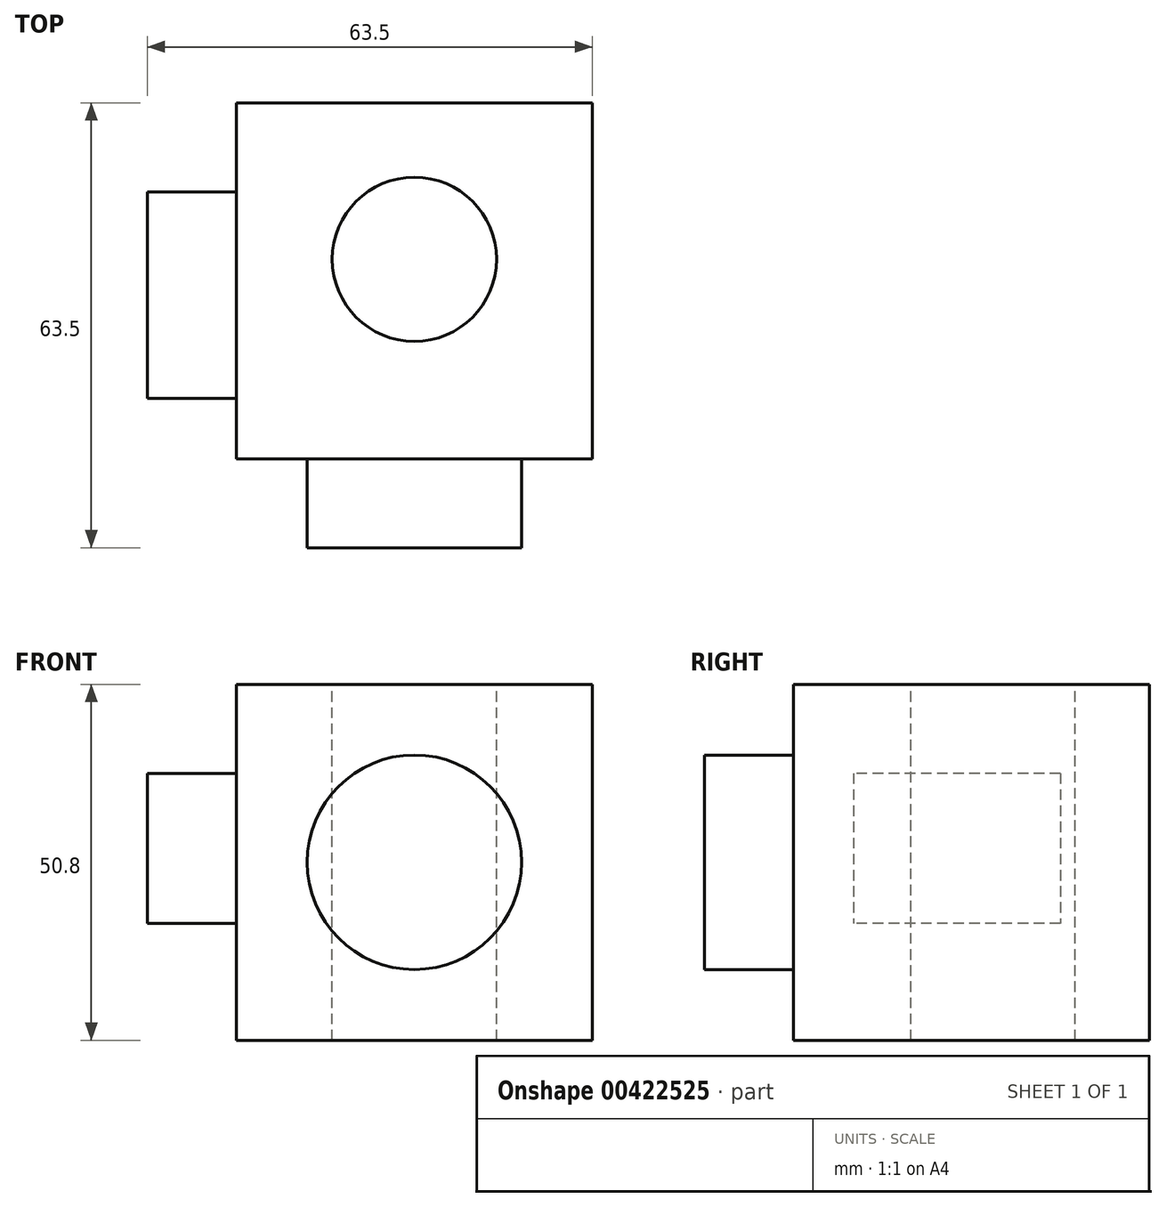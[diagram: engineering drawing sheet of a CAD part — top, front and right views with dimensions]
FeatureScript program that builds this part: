
annotation { "Feature Type Name" : "Feature", "Feature Type Description" : "" }
export const myFeature = defineFeature(function(context is Context, id is Id, definition is map)
    precondition{}
    {
        {
            var Q0;
            Q0=qCreatedBy(makeId("Front.planeOp"),FACE);
            var sketch = newSketch(context, id + "F0", { "sketchPlane" : qUnion([Q0])});
            skLineSegment(sketch, "E0", {"start": v(0, 0) * mm, "end": v(0, 50.8) * mm});
            skLineSegment(sketch, "E1", {"start": v(0, 50.8) * mm, "end": v(50.8, 50.8) * mm});
            skLineSegment(sketch, "E2", {"start": v(50.8, 50.8) * mm, "end": v(50.8, 0) * mm});
            skLineSegment(sketch, "E3", {"start": v(0, 0) * mm, "end": v(50.8, 0) * mm});
            skCircle(sketch, "E4", {"center": v(25.4, 25.4) * mm, "radius": 15.37 * mm});
            skSolve(sketch);
        }
        {
            var Q0;
            Q0=makeQuery(id+"F0.imprint","IMPRINT",FACE,{"disambiguationData":[TD([[makeQuery(id+"F0.imprint","IMPRINT",EDGE,{"derivedFrom":sQuery(id+"F0.wireOp",EDGE,"E4")}),1.0]])]});
            var Q1;
            Q1=makeQuery(id+"F0.imprint","IMPRINT",FACE,{"disambiguationData":[TD([[makeQuery(id+"F0.imprint","IMPRINT",EDGE,{"derivedFrom":sQuery(id+"F0.wireOp",EDGE,"E0")}),-1.0]])]});
            extrude(context, id + "F1", {"entities" : qUnion([Q0, Q1]), "depth" : 50.8 * mm});
        }
        {
            var Q0;
            Q0=qCreatedBy(makeId("Front.planeOp"),FACE);
            var sketch = newSketch(context, id + "F2", { "sketchPlane" : qUnion([Q0])});
            skCircle(sketch, "E5", {"center": v(25.4, 25.4) * mm, "radius": 15.3 * mm});
            skSolve(sketch);
        }
        {
            var Q0;
            Q0 = qSketchRegion(id + "F2", true);
            extrude(context, id + "F3", {"entities" : qUnion([Q0]), "operationType" : NewBodyOperationType.ADD, "depth" : 63.5 * mm});
        }
        {
            var Q0;
            Q0=makeQuery(id+"F1.opExtrude","SWEPT_FACE",FACE,{"disambiguationData":[OSD([sQuery(id+"F0.wireOp",EDGE,"E0")])]});
            var sketch = newSketch(context, id + "F4", { "sketchPlane" : qUnion([Q0])});
            skLineSegment(sketch, "E6.bottom", {"start": v(12.7, 38.1) * mm, "end": v(42.2, 38.1) * mm});
            skLineSegment(sketch, "E6.top", {"start": v(12.7, 16.66) * mm, "end": v(42.2, 16.66) * mm});
            skLineSegment(sketch, "E6.left", {"start": v(12.7, 38.1) * mm, "end": v(12.7, 16.66) * mm});
            skLineSegment(sketch, "E6.right", {"start": v(42.2, 38.1) * mm, "end": v(42.2, 16.66) * mm});
            skSolve(sketch);
        }
        {
            var Q0;
            Q0=makeQuery(id+"F4.imprint","IMPRINT",FACE,{"disambiguationData":[TD([[makeQuery(id+"F4.imprint","IMPRINT",EDGE,{"derivedFrom":sQuery(id+"F4.wireOp",EDGE,"E6.bottom")}),-1.0]])]});
            extrude(context, id + "F5", {"entities" : qUnion([Q0]), "operationType" : NewBodyOperationType.ADD, "depth" : 12.7 * mm});
        }
        {
            var Q0;
            Q0=makeQuery(id+"F1.opExtrude","SWEPT_FACE",FACE,{"disambiguationData":[OSD([sQuery(id+"F0.wireOp",EDGE,"E1")])]});
            var sketch = newSketch(context, id + "F6", { "sketchPlane" : qUnion([Q0])});
            skCircle(sketch, "E7", {"center": v(25.4, -22.34) * mm, "radius": 11.72 * mm});
            skSolve(sketch);
        }
        {
            var Q0;
            Q0=makeQuery(id+"F6.imprint","IMPRINT",FACE,{"disambiguationData":[TD([[makeQuery(id+"F6.imprint","IMPRINT",EDGE,{"derivedFrom":sQuery(id+"F6.wireOp",EDGE,"E7")}),1.0]])]});
            extrude(context, id + "F7", {"entities" : qUnion([Q0]), "operationType" : NewBodyOperationType.REMOVE, "oppositeDirection" : true, "depth" : 2540 * mm, "hasSecondDirection" : true, "secondDirectionOppositeDirection" : false, "secondDirectionDepth" : 25.4 * mm});
        }
    });
